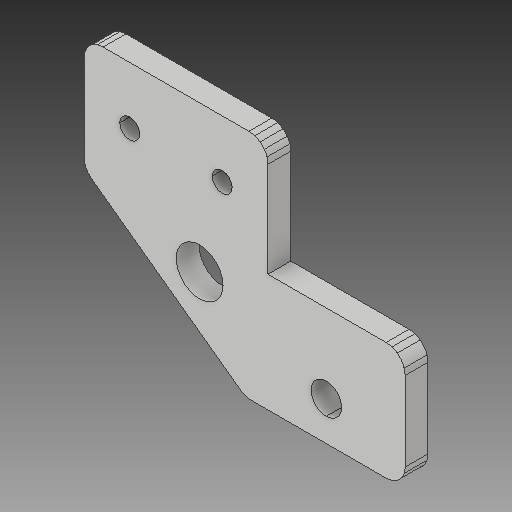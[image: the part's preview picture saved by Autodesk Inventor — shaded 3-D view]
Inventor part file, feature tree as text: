
AUTODESK INVENTOR PART (.ipt)
format: ipt  version: 2018 (Build 220112000, 112)  size: 235,008 bytes
history: native  units: mm
features: other x3, sketch x3
ambient origin geometry x8: Origin, YZ Plane, XZ Plane, XY Plane, X Axis, Y Axis, Z Axis, Center Point
bodies: Solid1 (feature_tree)
feature tree (6):
  other  "Leadscrew-rod-holder_MIR.ipt"
  other  "Solid1::Leadscrew-rod-holder_MIR.ipt"
  other  "TaggingFeature1"
  sketch  "Sketch1"  dims[d0=10.0mm]
  sketch  "Sketch2"
  sketch  "Sketch3"
